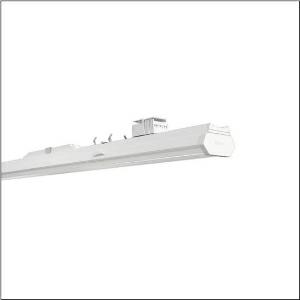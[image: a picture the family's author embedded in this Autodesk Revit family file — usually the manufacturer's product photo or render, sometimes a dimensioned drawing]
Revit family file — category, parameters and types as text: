
# Revit family: licross_r__21_protected_ho_52td12dn4c5l3c_f590
name_source: partatom
category: Lighting Fixtures
units: mm (PartAtom-declared; Revit-internal decimal feet)

## family parameters
Cut with Voids When Loaded = No
Host = Face
Light Source = No
Part Type = Normal
Room Calculation Point = No
Round Connector Dimension = Use Diameter
Shared = No

## types (1)
- --- (1 x LED, 810 lm, 4.8 W, 4000K)
    Apparent Load = 5 VA
    CIE Flux Codes = 70 91 97 98 100
    Color Rendering = 80
    Color Temperature = 4000K
    Default Elevation = 1800 mm
    Description = Licross® 21 Protected HO, luminaire insert, of sheet steel, galvanised, coil coated, white, length: 1.500mm, width: 90mm, height: 103mm, LED rated luminous flux: 12.810lm, light colour: 840, control gear: DALI 2, control gear: ECG DALI, with plug, 6-pole, with phase selection, for trunking rail, 14-core, mains connection: 220..240V, AC/DC, 0/50..60Hz, halogen-free wiring, for emergency light function, charging phase on R (wire number 6), converter,control gear: single battery element, battery: LiFeP04, 9Ah, primary optical cover: cover, of PMMA, light emission: direct with ceiling illumination distribution, protection rating (complete): IP54, insulation class (complete): insulation class I (protective earthing), certification: CE, UKCA, protection symbol: D if used in an environment with non-conductive dust loads with corresponding accessories, permissible ambient temperature for indoor applications: +5..+30°C, standard: EN 60598-2-22, corresponds to IFS (International Featured Standards) requirements for safety and quality in the food industry, reducing of maximum allowable ambient temperature of 5°C with ceiling mounting, LABS conformity tested according to VDMA 24364:2018-05, packaging unit: 1 piece
    Height = 92 mm
    Lamp = 1 x LED
    Lamp Light Flux = 810 lm
    Lamp Power = 4.8 W
    Lamp count = 1
    Length = 1500 mm
    Luminous efficacy = 169 lm/W
    Manufacturer = Siteco
    ModVariant = No
    Model = 52TD12DN4C5L3C
    Mounting Place = Ceiling
    Mounting Type = Pendant
    Number of Poles = 1
    OnlyDefault = Yes
    Power Factor = 1
    Product Name = Licross® 21 Protected HO
    Product group = luminaire insert
    ProductGroupID = 902
    Protection Class = Protection class I
    Protection Degree = IP 54
    RLX_Detail_Level = 1
    RlxData = <blob elided: 24809 chars, md5=f23abd29>
    Socket = socket
    Standby Power = 0 W
    System Light Flux = 810 lm
    System Power = 5 W
    Type Comments = : emergency light operation: 3 h
    Type Image = l_1256148.jpg
    URL = http://relux.com
    VarID = @adj_123609
    Voltage = 0 V
    Weight = 0.00 kg
    Width = 88 mm

## geometry (parser evidence)
native form markers: Blend x4, Sweep x12
no freeform markers — native parametric forms only
